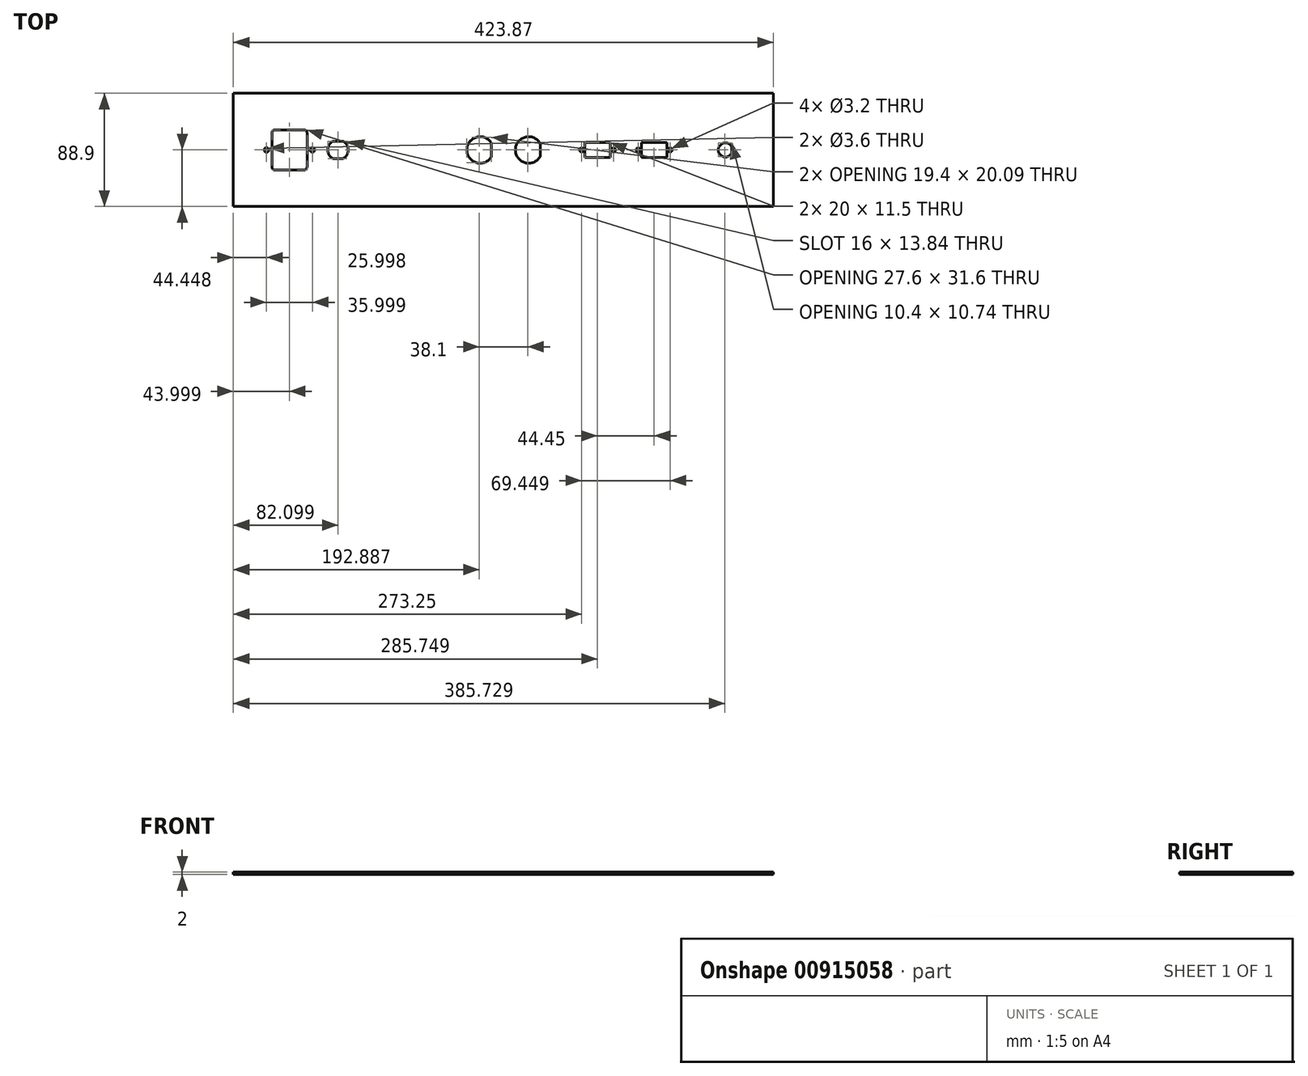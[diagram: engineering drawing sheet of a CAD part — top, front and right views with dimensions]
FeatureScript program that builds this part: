
annotation { "Feature Type Name" : "Feature", "Feature Type Description" : "" }
export const myFeature = defineFeature(function(context is Context, id is Id, definition is map)
    precondition{}
    {
        {
            var Q0;
            Q0=qCreatedBy(makeId("Top.planeOp"),FACE);
            var sketch = newSketch(context, id + "F0", { "sketchPlane" : qUnion([Q0])});
            skLineSegment(sketch, "E0.bottom", {"start": v(-191.7, -39.42) * mm, "end": v(232.18, -39.42) * mm});
            skLineSegment(sketch, "E0.top", {"start": v(-191.7, -128.32) * mm, "end": v(232.18, -128.32) * mm});
            skLineSegment(sketch, "E0.left", {"start": v(-191.7, -39.42) * mm, "end": v(-191.7, -128.32) * mm});
            skLineSegment(sketch, "E0.right", {"start": v(232.18, -39.42) * mm, "end": v(232.18, -128.32) * mm});
            skSolve(sketch);
        }
        {
            var Q0;
            Q0=makeQuery(id+"F0.imprint","IMPRINT",FACE,{"disambiguationData":[TD([[makeQuery(id+"F0.imprint","IMPRINT",EDGE,{"derivedFrom":sQuery(id+"F0.wireOp",EDGE,"E0.bottom")}),-1.0]])]});
            extrude(context, id + "F1", {"entities" : qUnion([Q0]), "depth" : 2 * mm, "offsetDistance" : 25.4 * mm});
        }
        {
            var Q0;
            Q0=makeQuery(id+"F1.opExtrude","CAP_FACE",FACE,{"disambiguationData":[OSD([sQuery(id+"F0.wireOp",EDGE,"E0.bottom"),sQuery(id+"F0.wireOp",EDGE,"E0.top"),sQuery(id+"F0.wireOp",EDGE,"E0.left"),sQuery(id+"F0.wireOp",EDGE,"E0.right")])],"isStart":false});
            var sketch = newSketch(context, id + "F2", { "sketchPlane" : qUnion([Q0])});
            skCircle(sketch, "E1", {"center": v(-109.6, -83.87) * mm, "radius": 8 * mm});
            skLineSegment(sketch, "E2", {"start": v(-105.58, -76.95) * mm, "end": v(-113.6, -76.95) * mm});
            skLineSegment(sketch, "E3", {"start": v(-113.6, -90.8) * mm, "end": v(-105.58, -90.8) * mm});
            skLineSegment(sketch, "E4.bottom", {"start": v(-136.3, -99.67) * mm, "end": v(-159.1, -99.67) * mm});
            skLineSegment(sketch, "E4.top", {"start": v(-136.3, -68.07) * mm, "end": v(-159.1, -68.07) * mm});
            skLineSegment(sketch, "E4.left", {"start": v(-133.9, -97.27) * mm, "end": v(-133.9, -70.47) * mm});
            skLineSegment(sketch, "E4.right", {"start": v(-161.5, -97.27) * mm, "end": v(-161.5, -70.47) * mm});
            skPoint(sketch, "E4.middle", {"position": v(-147.7, -83.87) * mm});
            skPoint(sketch, "E5.visualSharp", {"position": v(-133.9, -68.07) * mm});
            skArc(sketch, "E5.filletArc", {"start": v(-133.9, -70.47) * mm, "mid": v(-134.6, -68.78) * mm, "end": v(-136.3, -68.07) * mm});
            skPoint(sketch, "E6.visualSharp", {"position": v(-133.9, -99.67) * mm});
            skArc(sketch, "E6.filletArc", {"start": v(-136.3, -99.67) * mm, "mid": v(-134.6, -98.97) * mm, "end": v(-133.9, -97.27) * mm});
            skPoint(sketch, "E7.visualSharp", {"position": v(-161.5, -99.67) * mm});
            skArc(sketch, "E7.filletArc", {"start": v(-161.5, -97.27) * mm, "mid": v(-160.79, -98.97) * mm, "end": v(-159.1, -99.67) * mm});
            skPoint(sketch, "E8.visualSharp", {"position": v(-161.5, -68.07) * mm});
            skArc(sketch, "E8.filletArc", {"start": v(-159.1, -68.07) * mm, "mid": v(-160.79, -68.78) * mm, "end": v(-161.5, -70.47) * mm});
            skCircle(sketch, "E9", {"center": v(-165.7, -83.87) * mm, "radius": 1.8 * mm});
            skCircle(sketch, "E10", {"center": v(-129.7, -83.87) * mm, "radius": 1.8 * mm});
            skPoint(sketch, "E10.centerSnap0", {"position": v(-133.9, -83.87) * mm});
            skCircle(sketch, "E11", {"center": v(1.9, -83.87) * mm, "radius": 10.4 * mm});
            skLineSegment(sketch, "E12", {"start": v(10.9, -78.66) * mm, "end": v(10.9, -89.08) * mm});
            skCircle(sketch, "E13", {"center": v(40, -83.87) * mm, "radius": 10.4 * mm});
            skLineSegment(sketch, "E14", {"start": v(49, -78.66) * mm, "end": v(49, -89.08) * mm});
            skCircle(sketch, "E15", {"center": v(194.39, -83.87) * mm, "radius": 5.55 * mm});
            skLineSegment(sketch, "E16", {"start": v(199.24, -81.17) * mm, "end": v(199.24, -86.57) * mm});
            skLineSegment(sketch, "E17.bottom", {"start": v(104.06, -89.62) * mm, "end": v(84.06, -89.62) * mm});
            skLineSegment(sketch, "E17.top", {"start": v(104.06, -78.12) * mm, "end": v(84.06, -78.12) * mm});
            skLineSegment(sketch, "E17.left", {"start": v(104.06, -89.62) * mm, "end": v(104.06, -78.12) * mm});
            skLineSegment(sketch, "E17.right", {"start": v(84.06, -89.62) * mm, "end": v(84.06, -78.12) * mm});
            skPoint(sketch, "E17.middle", {"position": v(94.06, -83.87) * mm});
            skCircle(sketch, "E18", {"center": v(81.56, -83.87) * mm, "radius": 1.6 * mm});
            skCircle(sketch, "E19", {"center": v(106.56, -83.87) * mm, "radius": 1.6 * mm});
            skLineSegment(sketch, "E20.bottom", {"start": v(148.51, -89.62) * mm, "end": v(128.5, -89.62) * mm});
            skLineSegment(sketch, "E20.top", {"start": v(148.51, -78.12) * mm, "end": v(128.5, -78.12) * mm});
            skLineSegment(sketch, "E20.left", {"start": v(148.51, -89.62) * mm, "end": v(148.51, -78.12) * mm});
            skLineSegment(sketch, "E20.right", {"start": v(128.5, -89.62) * mm, "end": v(128.5, -78.12) * mm});
            skPoint(sketch, "E20.middle", {"position": v(138.5, -83.87) * mm});
            skCircle(sketch, "E21", {"center": v(126, -83.87) * mm, "radius": 1.6 * mm});
            skCircle(sketch, "E22", {"center": v(151, -83.87) * mm, "radius": 1.6 * mm});
            skSolve(sketch);
        }
        {
            var Q0;
            Q0=makeQuery(id+"F2.imprint","IMPRINT",FACE,{"disambiguationData":[TD([[makeQuery(id+"F2.imprint","IMPRINT",EDGE,{"derivedFrom":sQuery(id+"F2.wireOp",EDGE,"E9")}),1.0]])]});
            var Q1;
            Q1=makeQuery(id+"F2.imprint","IMPRINT",FACE,{"disambiguationData":[TD([[makeQuery(id+"F2.imprint","IMPRINT",EDGE,{"derivedFrom":sQuery(id+"F2.wireOp",EDGE,"E4.bottom")}),-1.0]])]});
            var Q2;
            Q2=makeQuery(id+"F2.imprint","IMPRINT",FACE,{"disambiguationData":[TD([[makeQuery(id+"F2.imprint","IMPRINT",EDGE,{"derivedFrom":sQuery(id+"F2.wireOp",EDGE,"E10")}),1.0]])]});
            var Q3;
            {var subQ0=sQuery(id+"F2.wireOp",EDGE,"E2");Q3=makeQuery(id+"F2.imprint","IMPRINT",FACE,{"disambiguationData":[TD([[makeQuery(id+"F2.imprint","IMPRINT",EDGE,{"derivedFrom":subQ0}),1.0]])]});}
            var Q4;
            {var subQ0=sQuery(id+"F2.wireOp",EDGE,"E12");Q4=makeQuery(id+"F2.imprint","IMPRINT",FACE,{"disambiguationData":[TD([[makeQuery(id+"F2.imprint","IMPRINT",EDGE,{"derivedFrom":subQ0}),-1.0]])]});}
            var Q5;
            {var subQ0=sQuery(id+"F2.wireOp",EDGE,"E14");Q5=makeQuery(id+"F2.imprint","IMPRINT",FACE,{"disambiguationData":[TD([[makeQuery(id+"F2.imprint","IMPRINT",EDGE,{"derivedFrom":subQ0}),-1.0]])]});}
            var Q6;
            {var subQ0=sQuery(id+"F2.wireOp",EDGE,"ZMNVGgwX-TyNH-TmWO-hqPt-VIMgWgPO2m3k");Q6=makeQuery(id+"F2.imprint","IMPRINT",FACE,{"disambiguationData":[TD([[makeQuery(id+"F2.imprint","IMPRINT",EDGE,{"derivedFrom":subQ0}),-1.0]])]});}
            var Q7;
            {var subQ0=sQuery(id+"F2.wireOp",EDGE,"E16");Q7=makeQuery(id+"F2.imprint","IMPRINT",FACE,{"disambiguationData":[TD([[makeQuery(id+"F2.imprint","IMPRINT",EDGE,{"derivedFrom":subQ0}),-1.0]])]});}
            var Q8;
            {var subQ0=sQuery(id+"F2.wireOp",EDGE,"gWUX13wx-6Jhi-x6pU-Wv1F-0fGEM20ZY8mr");Q8=makeQuery(id+"F2.imprint","IMPRINT",FACE,{"disambiguationData":[TD([[makeQuery(id+"F2.imprint","IMPRINT",EDGE,{"derivedFrom":subQ0}),-1.0]])]});}
            var Q9;
            Q9=makeQuery(id+"F2.imprint","IMPRINT",FACE,{"disambiguationData":[TD([[makeQuery(id+"F2.imprint","IMPRINT",EDGE,{"derivedFrom":sQuery(id+"F2.wireOp",EDGE,"E17.bottom")}),-1.0]])]});
            var Q10;
            Q10=makeQuery(id+"F2.imprint","IMPRINT",FACE,{"disambiguationData":[TD([[makeQuery(id+"F2.imprint","IMPRINT",EDGE,{"derivedFrom":sQuery(id+"F2.wireOp",EDGE,"E20.bottom")}),-1.0]])]});
            var Q11;
            Q11=makeQuery(id+"F2.imprint","IMPRINT",FACE,{"disambiguationData":[TD([[makeQuery(id+"F2.imprint","IMPRINT",EDGE,{"derivedFrom":sQuery(id+"F2.wireOp",EDGE,"E19")}),1.0]])]});
            var Q12;
            Q12=makeQuery(id+"F2.imprint","IMPRINT",FACE,{"disambiguationData":[TD([[makeQuery(id+"F2.imprint","IMPRINT",EDGE,{"derivedFrom":sQuery(id+"F2.wireOp",EDGE,"E18")}),1.0]])]});
            var Q13;
            Q13=makeQuery(id+"F2.imprint","IMPRINT",FACE,{"disambiguationData":[TD([[makeQuery(id+"F2.imprint","IMPRINT",EDGE,{"derivedFrom":sQuery(id+"F2.wireOp",EDGE,"E21")}),1.0]])]});
            var Q14;
            Q14=makeQuery(id+"F2.imprint","IMPRINT",FACE,{"disambiguationData":[TD([[makeQuery(id+"F2.imprint","IMPRINT",EDGE,{"derivedFrom":sQuery(id+"F2.wireOp",EDGE,"E22")}),1.0]])]});
            extrude(context, id + "F3", {"entities" : qUnion([Q0, Q1, Q2, Q3, Q4, Q5, Q6, Q7, Q8, Q9, Q10, Q11, Q12, Q13, Q14]), "operationType" : NewBodyOperationType.REMOVE, "oppositeDirection" : true, "depth" : 25.4 * mm, "offsetDistance" : 25.4 * mm});
        }
    });
